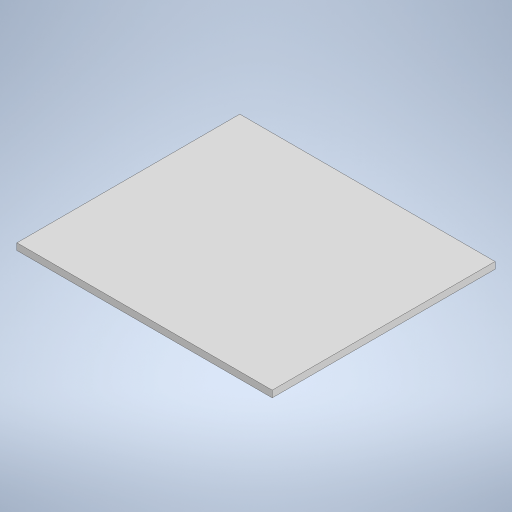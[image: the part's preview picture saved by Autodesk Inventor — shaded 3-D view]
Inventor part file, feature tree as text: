
AUTODESK INVENTOR PART (.ipt)
format: ipt  version: 2024.3 (Build 283343000, 343)  size: 201,216 bytes
history: native  units: mm
features: extrude x1, sketch x1
ambient origin geometry x8: Origin, YZ Plane, XZ Plane, XY Plane, X Axis, Y Axis, Z Axis, Center Point
bodies: Solid1 (feature_tree)
feature tree (2):
  extrude  "Extrusion1"  Depth=114.554mm
  sketch  "Sketch1"  dims[d0=100.0mm d1=114.554mm d2=3.0mm d3=0.0mm]
